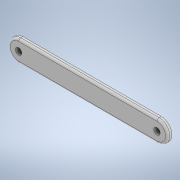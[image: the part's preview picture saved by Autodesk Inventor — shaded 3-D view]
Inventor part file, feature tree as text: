
AUTODESK INVENTOR PART (.ipt)
format: ipt  version: 2021.4 (Build 254397000, 397)  size: 123,904 bytes
history: native  units: mm
features: fillet x2, sketch x2, other x1, extrude x1, hole x1
ambient origin geometry x8: Origin, YZ Plane, XZ Plane, XY Plane, X Axis, Y Axis, Z Axis, Center Point
bodies: Body1 (feature_tree)
feature tree (7):
  other  "ソリッド1"
  extrude  "押し出し1"  Depth=150.0mm
  fillet  "フィレット1"  Radius=20.0mm
  fillet  "フィレット2"  Radius=4.0mm
  hole  "穴1"  [1 undecoded]
  sketch  "スケッチ1"
  sketch  "スケッチ2"
note: 1 required parameter value undecoded (feature->parameter linkage not recoverable at this tier; creation-order binding heuristic only, values carry confidence <= 0.55)
